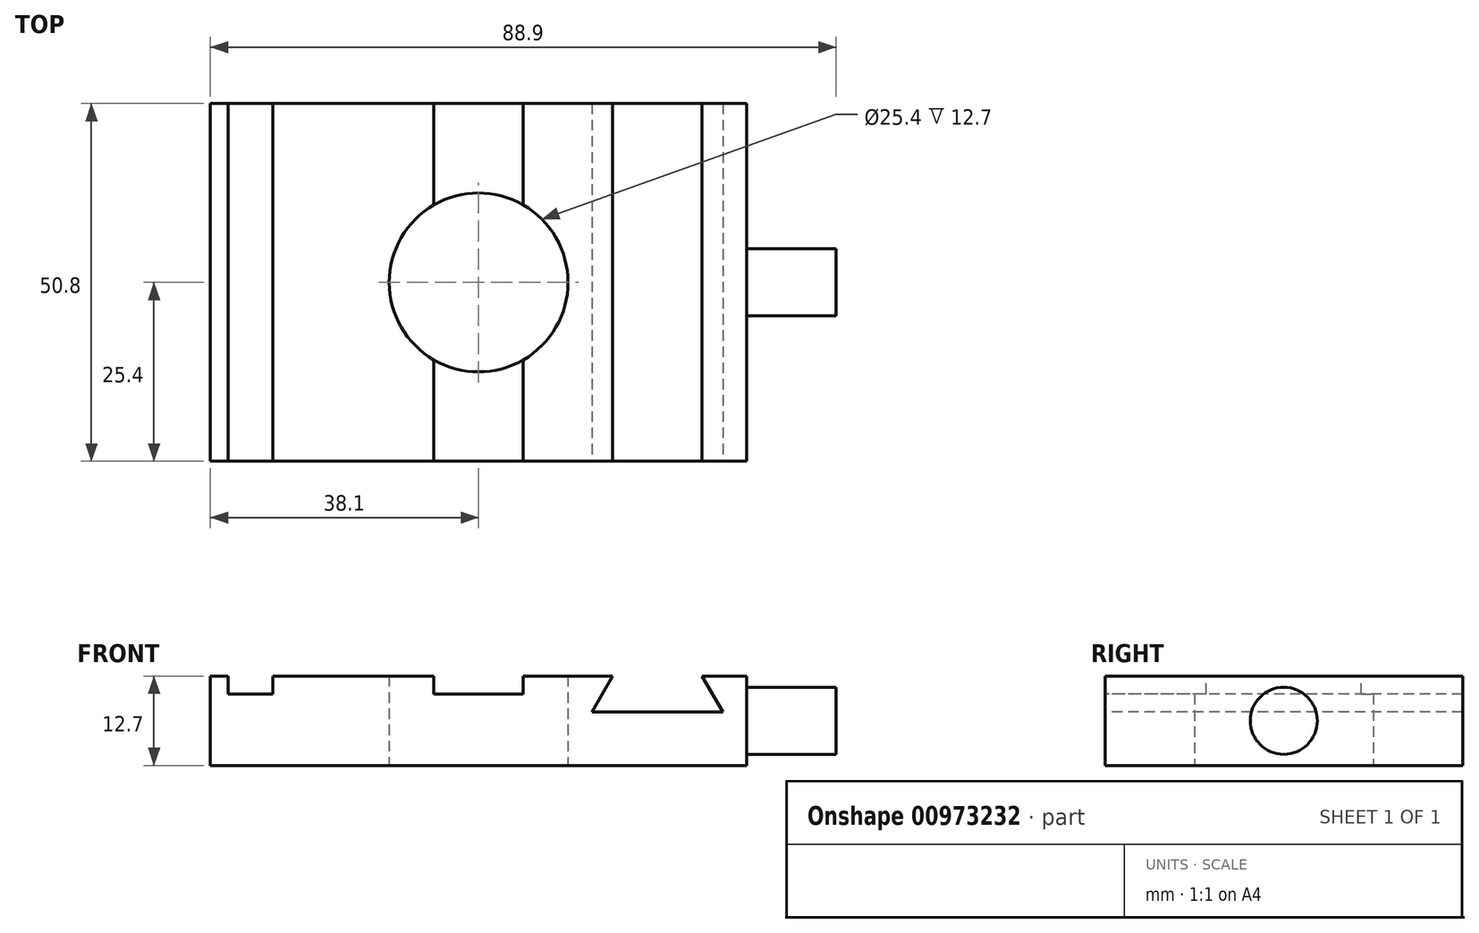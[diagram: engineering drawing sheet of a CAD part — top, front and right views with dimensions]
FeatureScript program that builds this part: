
annotation { "Feature Type Name" : "Feature", "Feature Type Description" : "" }
export const myFeature = defineFeature(function(context is Context, id is Id, definition is map)
    precondition{}
    {
        {
            var Q0;
            Q0=qCreatedBy(makeId("Top.planeOp"),FACE);
            var sketch = newSketch(context, id + "F0", { "sketchPlane" : qUnion([Q0])});
            skLineSegment(sketch, "E0.bottom", {"start": v(38.1, -25.4) * mm, "end": v(-38.1, -25.4) * mm});
            skLineSegment(sketch, "E0.top", {"start": v(38.1, 25.4) * mm, "end": v(-38.1, 25.4) * mm});
            skLineSegment(sketch, "E0.left", {"start": v(38.1, -25.4) * mm, "end": v(38.1, 25.4) * mm});
            skLineSegment(sketch, "E0.right", {"start": v(-38.1, -25.4) * mm, "end": v(-38.1, 25.4) * mm});
            skPoint(sketch, "E0.middle", {"position": v(0, 0) * mm});
            skCircle(sketch, "E1", {"center": v(0, 0) * mm, "radius": 12.7 * mm});
            skSolve(sketch);
        }
        {
            var Q0;
            Q0=makeQuery(id+"F0.imprint","IMPRINT",FACE,{"disambiguationData":[TD([[makeQuery(id+"F0.imprint","IMPRINT",EDGE,{"derivedFrom":sQuery(id+"F0.wireOp",EDGE,"E0.bottom")}),-1.0]])]});
            extrude(context, id + "F1", {"entities" : qUnion([Q0]), "depth" : 12.7 * mm, "offsetDistance" : 25.4 * mm});
        }
        {
            var Q0;
            Q0=makeQuery(id+"F1.opExtrude","CAP_FACE",FACE,{"disambiguationData":[OSD([sQuery(id+"F0.wireOp",EDGE,"E0.bottom"),sQuery(id+"F0.wireOp",EDGE,"E0.top"),sQuery(id+"F0.wireOp",EDGE,"E0.left"),sQuery(id+"F0.wireOp",EDGE,"E0.right"),sQuery(id+"F0.wireOp",EDGE,"E1")])],"isStart":false});
            var sketch = newSketch(context, id + "F2", { "sketchPlane" : qUnion([Q0])});
            skLineSegment(sketch, "E2.bottom", {"start": v(-35.56, 25.4) * mm, "end": v(-29.21, 25.4) * mm});
            skLineSegment(sketch, "E2.top", {"start": v(-35.56, -25.4) * mm, "end": v(-29.21, -25.4) * mm});
            skLineSegment(sketch, "E2.left", {"start": v(-35.56, 25.4) * mm, "end": v(-35.56, -25.4) * mm});
            skLineSegment(sketch, "E2.right", {"start": v(-29.21, 25.4) * mm, "end": v(-29.21, -25.4) * mm});
            skLineSegment(sketch, "E3", {"start": v(-6.35, 25.4) * mm, "end": v(-6.35, -25.4) * mm});
            skLineSegment(sketch, "E4", {"start": v(-6.35, -25.4) * mm, "end": v(6.35, -25.4) * mm});
            skLineSegment(sketch, "E5", {"start": v(6.35, -25.4) * mm, "end": v(6.35, 25.4) * mm});
            skLineSegment(sketch, "E6", {"start": v(6.35, 25.4) * mm, "end": v(-6.35, 25.4) * mm});
            skLineSegment(sketch, "E7", {"start": v(0, 25.4) * mm, "end": v(0, -25.4) * mm, "construction": true});
            skPoint(sketch, "E8", {"position": v(0, 0) * mm});
            skSolve(sketch);
        }
        {
            var Q0;
            Q0=makeQuery(id+"F2.imprint","IMPRINT",FACE,{"disambiguationData":[TD([[makeQuery(id+"F2.imprint","IMPRINT",EDGE,{"derivedFrom":sQuery(id+"F2.wireOp",EDGE,"E2.bottom")}),1.0]])]});
            var Q1;
            {var subQ0=sQuery(id+"F2.wireOp",EDGE,"E4");Q1=makeQuery(id+"F2.imprint","IMPRINT",FACE,{"disambiguationData":[TD([[makeQuery(id+"F2.imprint","IMPRINT",EDGE,{"derivedFrom":subQ0}),-1.0]])]});}
            var Q2;
            {var subQ0=sQuery(id+"F2.wireOp",EDGE,"E6");Q2=makeQuery(id+"F2.imprint","IMPRINT",FACE,{"disambiguationData":[TD([[makeQuery(id+"F2.imprint","IMPRINT",EDGE,{"derivedFrom":subQ0}),1.0]])]});}
            extrude(context, id + "F3", {"entities" : qUnion([Q0, Q1, Q2]), "operationType" : NewBodyOperationType.REMOVE, "oppositeDirection" : true, "depth" : 2.54 * mm, "offsetDistance" : 25.4 * mm});
        }
        {
            var Q0;
            Q0=makeQuery(id+"F1.opExtrude","SWEPT_FACE",FACE,{"disambiguationData":[OSD([sQuery(id+"F0.wireOp",EDGE,"E0.bottom")])]});
            var sketch = newSketch(context, id + "F4", { "sketchPlane" : qUnion([Q0])});
            skLineSegment(sketch, "E9", {"start": v(19.05, 12.7) * mm, "end": v(16.12, 7.62) * mm});
            skLineSegment(sketch, "E10", {"start": v(16.12, 7.62) * mm, "end": v(34.68, 7.62) * mm});
            skLineSegment(sketch, "E11", {"start": v(34.68, 7.62) * mm, "end": v(31.75, 12.7) * mm});
            skLineSegment(sketch, "E12", {"start": v(31.75, 12.7) * mm, "end": v(19.05, 12.7) * mm});
            skLineSegment(sketch, "E13", {"start": v(25.4, 7.62) * mm, "end": v(25.4, 12.7) * mm, "construction": true});
            skSolve(sketch);
        }
        {
            var Q0;
            Q0=makeQuery(id+"F4.imprint","IMPRINT",FACE,{"disambiguationData":[TD([[makeQuery(id+"F4.imprint","IMPRINT",EDGE,{"derivedFrom":sQuery(id+"F4.wireOp",EDGE,"E9")}),1.0]])]});
            extrude(context, id + "F5", {"entities" : qUnion([Q0]), "operationType" : NewBodyOperationType.REMOVE, "endBound" : BoundingType.THROUGH_ALL, "oppositeDirection" : true, "depth" : 25.4 * mm, "offsetDistance" : 25.4 * mm});
        }
        {
            var Q0;
            Q0=makeQuery(id+"F1.opExtrude","SWEPT_FACE",FACE,{"disambiguationData":[OSD([sQuery(id+"F0.wireOp",EDGE,"E0.left")])]});
            var sketch = newSketch(context, id + "F6", { "sketchPlane" : qUnion([Q0])});
            skCircle(sketch, "E14", {"center": v(0, 6.35) * mm, "radius": 4.76 * mm});
            skPoint(sketch, "E14.centerSnap0", {"position": v(-25.4, 6.35) * mm});
            skPoint(sketch, "E14.centerSnap1", {"position": v(0, 12.7) * mm});
            skSolve(sketch);
        }
        {
            var Q0;
            Q0=makeQuery(id+"F6.imprint","IMPRINT",FACE,{"disambiguationData":[TD([[makeQuery(id+"F6.imprint","IMPRINT",EDGE,{"derivedFrom":sQuery(id+"F6.wireOp",EDGE,"E14")}),1.0]])]});
            extrude(context, id + "F7", {"entities" : qUnion([Q0]), "operationType" : NewBodyOperationType.ADD, "depth" : 12.7 * mm, "offsetDistance" : 25.4 * mm});
        }
    });
